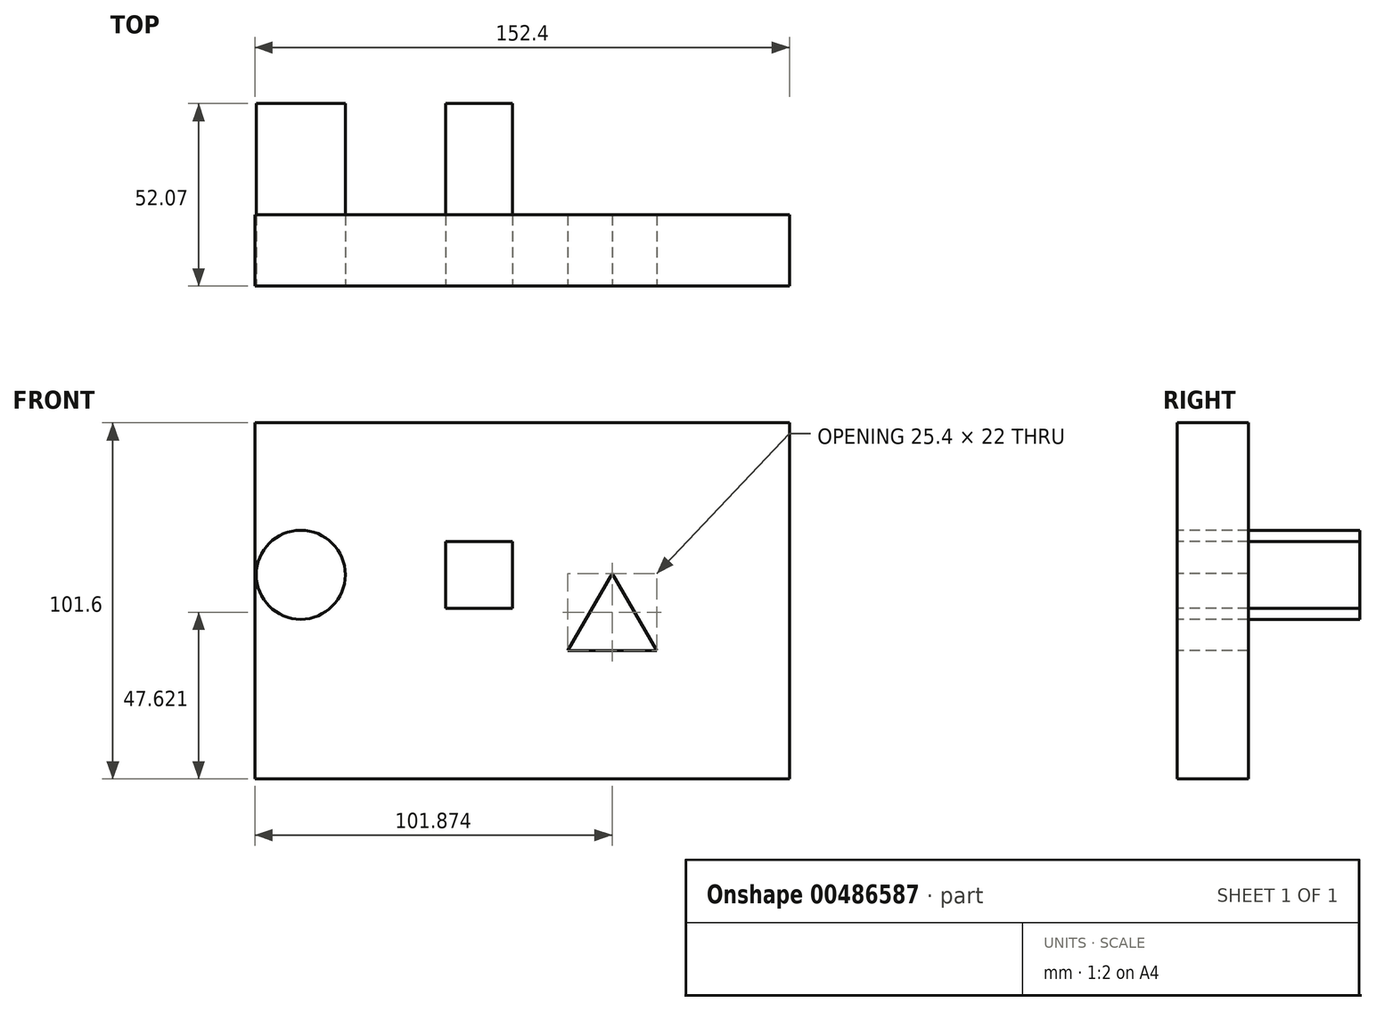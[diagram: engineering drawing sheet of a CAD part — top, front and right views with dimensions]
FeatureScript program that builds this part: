
annotation { "Feature Type Name" : "Feature", "Feature Type Description" : "" }
export const myFeature = defineFeature(function(context is Context, id is Id, definition is map)
    precondition{}
    {
        {
            var Q0;
            Q0=qCreatedBy(makeId("Front.planeOp"),FACE);
            var sketch = newSketch(context, id + "F0", { "sketchPlane" : qUnion([Q0])});
            skLineSegment(sketch, "E0.bottom", {"start": v(-95.65, 43.32) * mm, "end": v(56.75, 43.32) * mm});
            skLineSegment(sketch, "E0.top", {"start": v(-95.65, -58.28) * mm, "end": v(56.75, -58.28) * mm});
            skLineSegment(sketch, "E0.left", {"start": v(-95.65, 43.32) * mm, "end": v(-95.65, -58.28) * mm});
            skLineSegment(sketch, "E0.right", {"start": v(56.75, 43.32) * mm, "end": v(56.75, -58.28) * mm});
            skSolve(sketch);
        }
        {
            var Q0;
            Q0 = qSketchRegion(id + "F0", true);
            extrude(context, id + "F1", {"entities" : qUnion([Q0]), "depth" : 20.32 * mm});
        }
        {
            var Q0;
            Q0=makeQuery(id+"F1.opExtrude","CAP_FACE",FACE,{"disambiguationData":[OSD([sQuery(id+"F0.wireOp",EDGE,"E0.bottom"),sQuery(id+"F0.wireOp",EDGE,"E0.top"),sQuery(id+"F0.wireOp",EDGE,"E0.left"),sQuery(id+"F0.wireOp",EDGE,"E0.right")])],"isStart":false});
            var sketch = newSketch(context, id + "F2", { "sketchPlane" : qUnion([Q0])});
            skLineSegment(sketch, "E1", {"start": v(0, 0) * mm, "end": v(6.35, 0) * mm});
            skPoint(sketch, "E2.endSnap0", {"position": v(3.18, 0) * mm});
            skLineSegment(sketch, "E3", {"start": v(6.22, 0.34) * mm, "end": v(-6.48, -21.66) * mm});
            skLineSegment(sketch, "E4", {"start": v(-6.48, -21.66) * mm, "end": v(6.22, 0.34) * mm});
            skLineSegment(sketch, "E5", {"start": v(6.22, 0.34) * mm, "end": v(18.92, -21.66) * mm});
            skLineSegment(sketch, "E6", {"start": v(18.92, -21.66) * mm, "end": v(-6.48, -21.66) * mm});
            skLineSegment(sketch, "E7", {"start": v(0, 0) * mm, "end": v(-31.75, 0) * mm});
            skLineSegment(sketch, "E8.bottom", {"start": v(-22.23, -9.53) * mm, "end": v(-41.27, -9.53) * mm});
            skLineSegment(sketch, "E8.top", {"start": v(-22.23, 9.53) * mm, "end": v(-41.27, 9.53) * mm});
            skLineSegment(sketch, "E8.left", {"start": v(-22.22, -9.53) * mm, "end": v(-22.23, 9.53) * mm});
            skLineSegment(sketch, "E8.right", {"start": v(-41.27, -9.52) * mm, "end": v(-41.27, 9.53) * mm});
            skPoint(sketch, "E8.middle", {"position": v(-31.75, 0) * mm});
            skLineSegment(sketch, "E9", {"start": v(-31.75, 0) * mm, "end": v(-82.55, 0) * mm});
            skCircle(sketch, "E10", {"center": v(-82.55, 0) * mm, "radius": 12.7 * mm});
            skSolve(sketch);
        }
        {
            var Q0;
            Q0=makeQuery(id+"F2.imprint","IMPRINT",FACE,{"disambiguationData":[TD([[makeQuery(id+"F2.imprint","IMPRINT",EDGE,{"derivedFrom":sQuery(id+"F2.wireOp",EDGE,"E10")}),1.0]])]});
            var Q1;
            {var subQ1=sQuery(id+"F2.wireOp",EDGE,"E8.bottom");Q1=makeQuery(id+"F2.imprint","IMPRINT",FACE,{"disambiguationData":[TD([[makeQuery(id+"F2.imprint","IMPRINT",EDGE,{"derivedFrom":subQ1}),-1.0]])]});}
            var Q2;
            {var subQ1=sQuery(id+"F2.wireOp",EDGE,"E8.top");Q2=makeQuery(id+"F2.imprint","IMPRINT",FACE,{"disambiguationData":[TD([[makeQuery(id+"F2.imprint","IMPRINT",EDGE,{"derivedFrom":subQ1}),1.0]])]});}
            var Q3;
            Q3=sQuery(id+"F2.wireOp",EDGE,"E10");
            var Q4;
            Q4=sQuery(id+"F2.wireOp",EDGE,"E8.bottom");
            var Q5;
            Q5=sQuery(id+"F2.wireOp",EDGE,"E8.left");
            var Q6;
            Q6=sQuery(id+"F2.wireOp",EDGE,"E8.top");
            var Q7;
            Q7=sQuery(id+"F2.wireOp",EDGE,"E8.right");
            extrude(context, id + "F3", {"entities" : qUnion([Q0, Q1, Q2]), "surfaceEntities" : qUnion([Q3, Q4, Q5, Q6, Q7]), "oppositeDirection" : true, "depth" : 52.07 * mm});
        }
        {
            var Q0;
            {var subQ3=sQuery(id+"F2.wireOp",EDGE,"E5");Q0=makeQuery(id+"F2.imprint","IMPRINT",FACE,{"disambiguationData":[TD([[makeQuery(id+"F2.imprint","IMPRINT",EDGE,{"derivedFrom":subQ3}),-1.0]])]});}
            extrude(context, id + "F4", {"entities" : qUnion([Q0]), "operationType" : NewBodyOperationType.REMOVE, "oppositeDirection" : true, "depth" : 25.4 * mm});
        }
    });
